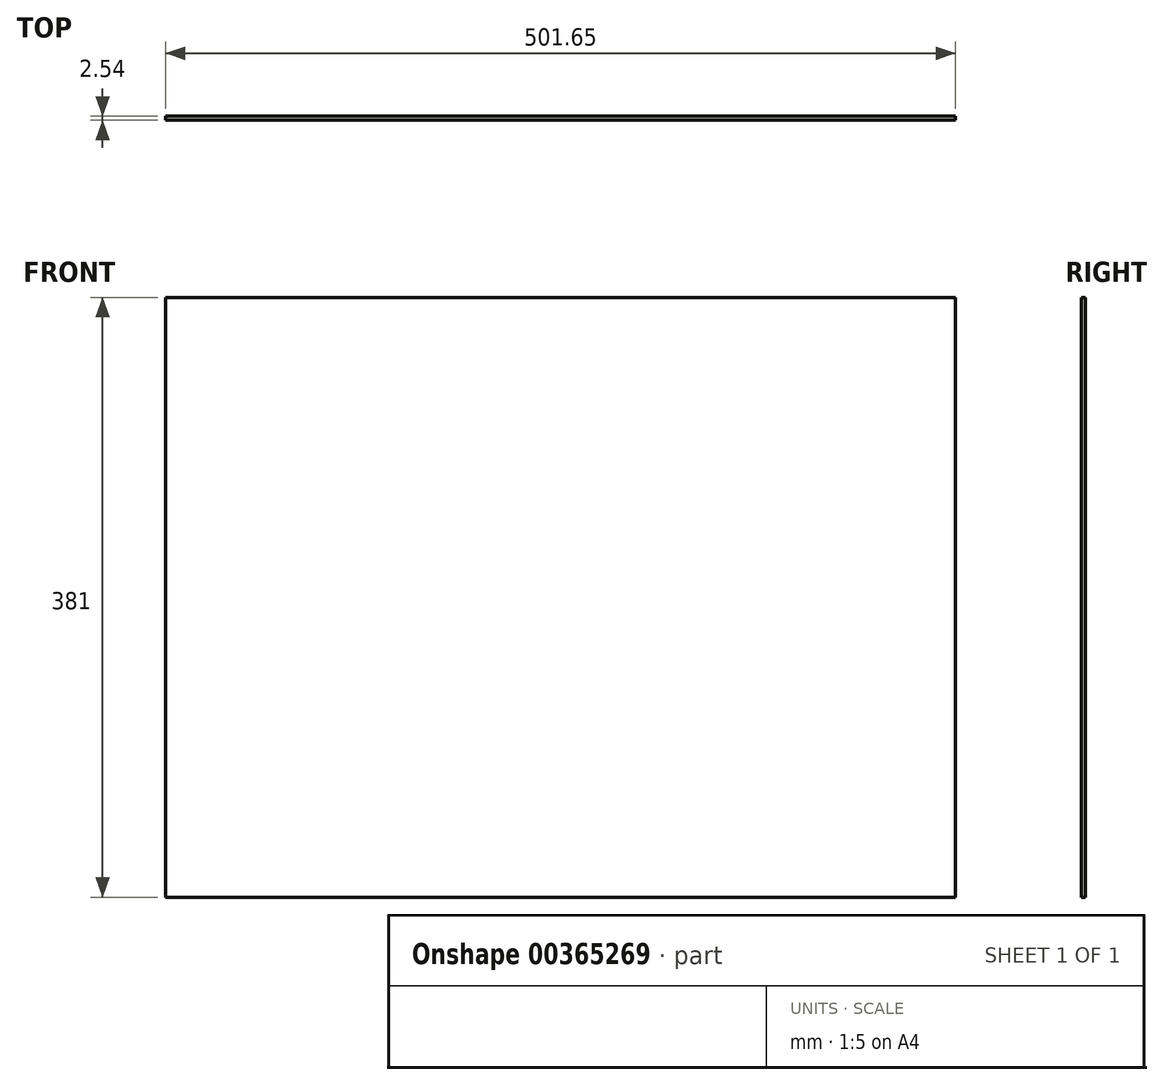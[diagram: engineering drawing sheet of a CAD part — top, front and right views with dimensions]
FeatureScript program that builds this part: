
annotation { "Feature Type Name" : "Feature", "Feature Type Description" : "" }
export const myFeature = defineFeature(function(context is Context, id is Id, definition is map)
    precondition{}
    {
        {
            var Q0;
            Q0=qCreatedBy(makeId("Front.planeOp"),FACE);
            var sketch = newSketch(context, id + "F0", { "sketchPlane" : qUnion([Q0])});
            skLineSegment(sketch, "E0", {"start": v(-222.9, 241.08) * mm, "end": v(278.74, 241.08) * mm});
            skLineSegment(sketch, "E1", {"start": v(278.74, 241.08) * mm, "end": v(278.74, -139.92) * mm});
            skLineSegment(sketch, "E2", {"start": v(-222.9, -139.92) * mm, "end": v(278.74, -139.92) * mm});
            skLineSegment(sketch, "E3", {"start": v(-222.9, 241.08) * mm, "end": v(-222.9, -139.92) * mm});
            skSolve(sketch);
        }
        {
            var Q0;
            Q0=qSketchRegion(id+"F0",true);
            extrude(context, id + "F1", {"entities" : qUnion([Q0]), "depth" : 2.54 * mm});
        }
    });
